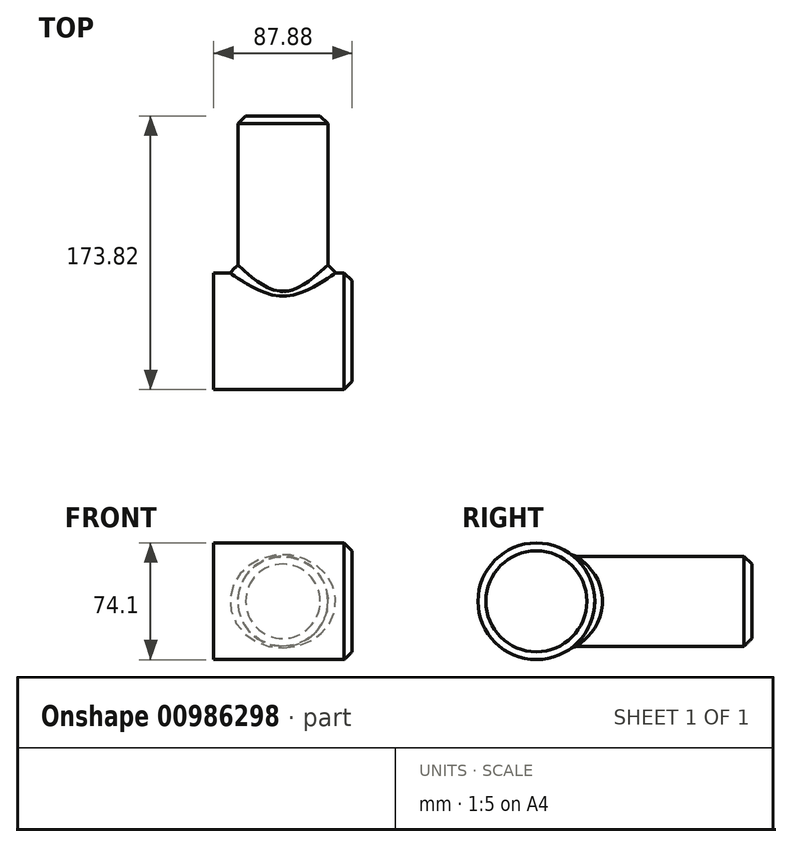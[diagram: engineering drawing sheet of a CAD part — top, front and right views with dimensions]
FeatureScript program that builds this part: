
annotation { "Feature Type Name" : "Feature", "Feature Type Description" : "" }
export const myFeature = defineFeature(function(context is Context, id is Id, definition is map)
    precondition{}
    {
        {
            var Q0;
            Q0=qCreatedBy(makeId("Right.planeOp"),FACE);
            var sketch = newSketch(context, id + "F0", { "sketchPlane" : qUnion([Q0])});
            skCircle(sketch, "E0", {"center": v(0, 0) * mm, "radius": 37.05 * mm});
            skSolve(sketch);
        }
        {
            var Q0;
            Q0=makeQuery(id+"F0.imprint","IMPRINT",FACE,{"disambiguationData":[TD([[makeQuery(id+"F0.imprint","IMPRINT",EDGE,{"derivedFrom":sQuery(id+"F0.wireOp",EDGE,"E0")}),1.0]])]});
            extrude(context, id + "F1", {"entities" : qUnion([Q0]), "endBound" : BoundingType.SYMMETRIC, "depth" : 87.88 * mm, "offsetDistance" : 25.4 * mm});
        }
        {
            var Q0;
            Q0=qCreatedBy(makeId("Front.planeOp"),FACE);
            var sketch = newSketch(context, id + "F2", { "sketchPlane" : qUnion([Q0])});
            skCircle(sketch, "E1", {"center": v(0, 0) * mm, "radius": 28.62 * mm});
            skSolve(sketch);
        }
        {
            var Q0;
            Q0 = qSketchRegion(id + "F2", true);
            extrude(context, id + "F3", {"entities" : qUnion([Q0]), "operationType" : NewBodyOperationType.ADD, "endBound" : BoundingType.THROUGH_ALL, "oppositeDirection" : true, "depth" : 25 * mm, "hasOffset" : true, "offsetDistance" : 3 * mm, "offsetOppositeDirection" : true});
        }
        {
            var Q0;
            Q0=makeQuery(id+"F3.opExtrude","SWEPT_FACE",FACE,{"disambiguationData":[OSD([sQuery(id+"F2.wireOp",EDGE,"E1")])]});
            var Q1;
            Q1=makeQuery(id+"F1.opExtrude","CAP_EDGE",EDGE,{"disambiguationData":[OSD([sQuery(id+"F0.wireOp",EDGE,"E0")])],"isStart":false});
            chamfer(context, id + "F4", {"entities" : qUnion([Q0, Q1]), "width" : 5 * mm, "tangentPropagation" : true});
        }
    });
